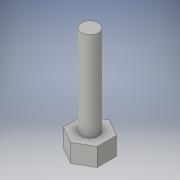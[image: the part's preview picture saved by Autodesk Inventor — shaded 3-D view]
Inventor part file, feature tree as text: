
AUTODESK INVENTOR PART (.ipt)
format: ipt  version: 2016 (Build 200138000, 138)  size: 99,840 bytes
history: native  units: in
note: dims shown in document units (in); Inventor stores cm internally (conversion verified against a paired STEP export)
features: extrude x2, sketch x2
ambient origin geometry x8: Origin, YZ Plane, XZ Plane, XY Plane, X Axis, Y Axis, Z Axis, Center Point
bodies: Solid1 (feature_tree)
feature tree (4):
  extrude  "Extrusion1"  Depth=0.203in TaperAngle=0.0deg
  extrude  "Extrusion2"  Depth=1.0in TaperAngle=0.0deg
  sketch  "Sketch1"  dims[d0=0.375in d1=0.203in d2=0.0in]
  sketch  "Sketch2"  dims[d3=0.19in d4=1.0in d5=0.0in]
